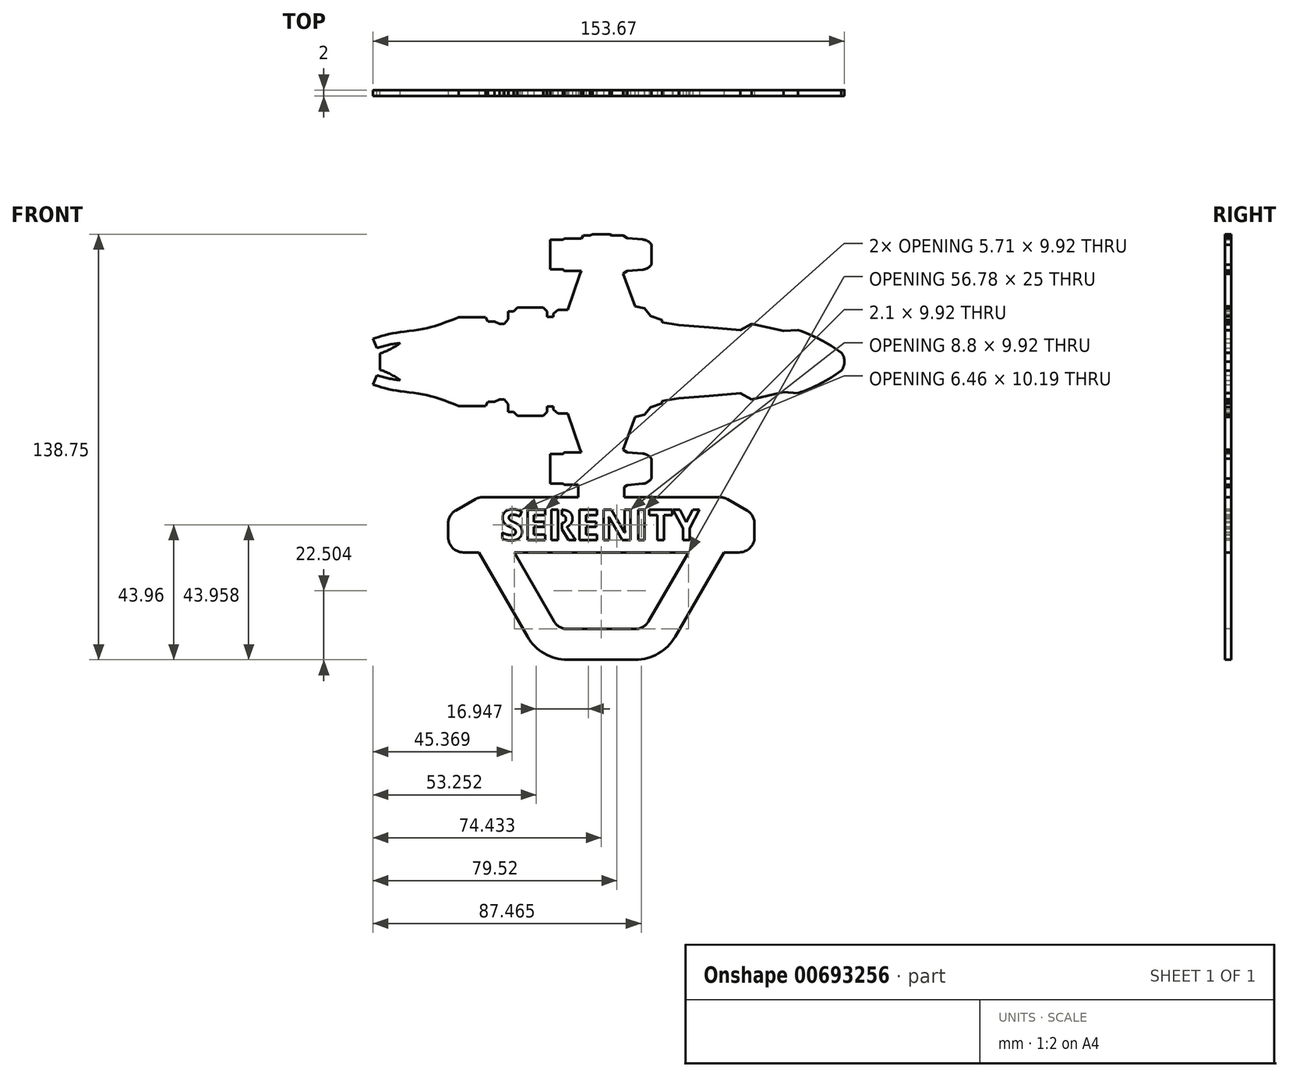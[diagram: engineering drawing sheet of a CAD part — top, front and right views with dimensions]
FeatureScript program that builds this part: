
annotation { "Feature Type Name" : "Feature", "Feature Type Description" : "" }
export const myFeature = defineFeature(function(context is Context, id is Id, definition is map)
    precondition{}
    {
        {
            var Q0;
            Q0=qCreatedBy(makeId("Front.planeOp"),FACE);
            var sketch = newSketch(context, id + "F0", { "sketchPlane" : qUnion([Q0])});
            skLineSegment(sketch, "E0", {"start": v(7.53, 23.83) * mm, "end": v(10.74, 15.17) * mm});
            skLineSegment(sketch, "E1", {"start": v(10.74, 15.17) * mm, "end": v(13.2, 14.62) * mm});
            skLineSegment(sketch, "E2", {"start": v(13.2, 14.62) * mm, "end": v(14.85, 12.63) * mm});
            skLineSegment(sketch, "E3", {"start": v(14.85, 12.63) * mm, "end": v(17.8, 11.6) * mm});
            skLineSegment(sketch, "E4", {"start": v(17.8, 11.6) * mm, "end": v(17.8, 10.91) * mm});
            skLineSegment(sketch, "E5", {"start": v(17.8, 10.91) * mm, "end": v(22.32, 10.23) * mm});
            skLineSegment(sketch, "E6", {"start": v(22.32, 10.23) * mm, "end": v(30.34, 9.58) * mm});
            skLineSegment(sketch, "E7", {"start": v(30.34, 9.58) * mm, "end": v(38.57, 8.93) * mm});
            skLineSegment(sketch, "E8", {"start": v(38.57, 8.93) * mm, "end": v(41.59, 10.56) * mm});
            skLineSegment(sketch, "E9", {"start": v(41.59, 10.56) * mm, "end": v(50.03, 8.63) * mm});
            skLineSegment(sketch, "E10", {"start": v(50.03, 8.63) * mm, "end": v(53.89, 8.9) * mm});
            skArc(sketch, "E11", {"start": v(65.33, 2.94) * mm, "mid": v(59.83, 6.35) * mm, "end": v(53.89, 8.9) * mm});
            skLineSegment(sketch, "E12", {"start": v(66.18, 0.52) * mm, "end": v(-57.02, 0.52) * mm, "construction": true});
            skArc(sketch, "E13", {"start": v(66.18, 0.52) * mm, "mid": v(65.97, 1.8) * mm, "end": v(65.33, 2.94) * mm});
            skLineSegment(sketch, "E14", {"start": v(7.53, 23.83) * mm, "end": v(8.61, 24.57) * mm});
            skLineSegment(sketch, "E15", {"start": v(8.61, 24.57) * mm, "end": v(12.67, 24.9) * mm});
            skArc(sketch, "E16", {"start": v(12.67, 24.9) * mm, "mid": v(14.02, 25.31) * mm, "end": v(15.04, 26.27) * mm});
            skLineSegment(sketch, "E17", {"start": v(15.04, 26.27) * mm, "end": v(15.04, 31.51) * mm});
            skLineSegment(sketch, "E18", {"start": v(15.04, 28.9) * mm, "end": v(-12.08, 28.9) * mm, "construction": true});
            skLineSegment(sketch, "E19", {"start": v(-3.95, 23.65) * mm, "end": v(-7.16, 14.3) * mm});
            skLineSegment(sketch, "E20", {"start": v(-3.95, 23.65) * mm, "end": v(-3.57, 24.6) * mm});
            skLineSegment(sketch, "E21", {"start": v(-3.57, 24.6) * mm, "end": v(-8.07, 24.6) * mm});
            skLineSegment(sketch, "E22", {"start": v(-8.07, 24.6) * mm, "end": v(-8.43, 24.95) * mm});
            skLineSegment(sketch, "E23", {"start": v(-8.43, 24.95) * mm, "end": v(-11.74, 24.95) * mm});
            skLineSegment(sketch, "E24", {"start": v(-11.74, 24.95) * mm, "end": v(-11.74, 32.83) * mm});
            skArc(sketch, "E25.MirrorCS", {"start": v(12.67, 32.9) * mm, "mid": v(14.02, 32.47) * mm, "end": v(15.04, 31.51) * mm});
            skLineSegment(sketch, "E26.MirrorCS", {"start": v(8.61, 33.21) * mm, "end": v(12.67, 32.9) * mm});
            skLineSegment(sketch, "E27.MirrorCS", {"start": v(7.53, 33.95) * mm, "end": v(8.61, 33.21) * mm});
            skLineSegment(sketch, "E28.MirrorCS", {"start": v(-3.57, 33.2) * mm, "end": v(-8.07, 33.2) * mm});
            skLineSegment(sketch, "E29.MirrorCS", {"start": v(-8.43, 32.83) * mm, "end": v(-11.74, 32.83) * mm});
            skLineSegment(sketch, "E30.MirrorCS", {"start": v(-8.07, 33.2) * mm, "end": v(-8.43, 32.83) * mm});
            skLineSegment(sketch, "E31", {"start": v(7.53, 33.95) * mm, "end": v(4.55, 33.95) * mm});
            skLineSegment(sketch, "E32", {"start": v(4.55, 33.95) * mm, "end": v(4, 34.32) * mm});
            skLineSegment(sketch, "E33", {"start": v(4, 34.32) * mm, "end": v(-0.49, 34.32) * mm});
            skLineSegment(sketch, "E34", {"start": v(-0.49, 34.32) * mm, "end": v(-1.24, 33.95) * mm});
            skLineSegment(sketch, "E35", {"start": v(-1.24, 33.95) * mm, "end": v(-3, 33.95) * mm});
            skLineSegment(sketch, "E36", {"start": v(-3, 33.95) * mm, "end": v(-3.57, 33.2) * mm});
            skLineSegment(sketch, "E37", {"start": v(-7.16, 14.3) * mm, "end": v(-9.7, 14.3) * mm});
            skLineSegment(sketch, "E38", {"start": v(-9.7, 14.3) * mm, "end": v(-10.96, 13.27) * mm});
            skLineSegment(sketch, "E39", {"start": v(-10.96, 13.27) * mm, "end": v(-10.96, 12.44) * mm});
            skLineSegment(sketch, "E40", {"start": v(-10.96, 12.44) * mm, "end": v(-12.6, 12.44) * mm});
            skLineSegment(sketch, "E41", {"start": v(-12.6, 12.44) * mm, "end": v(-12.6, 13.85) * mm});
            skLineSegment(sketch, "E42", {"start": v(-12.6, 13.85) * mm, "end": v(-13.62, 14.92) * mm});
            skLineSegment(sketch, "E43", {"start": v(-13.62, 14.92) * mm, "end": v(-20.41, 14.92) * mm});
            skLineSegment(sketch, "E44", {"start": v(-20.41, 14.92) * mm, "end": v(-21.53, 13.85) * mm});
            skLineSegment(sketch, "E45", {"start": v(-21.53, 13.85) * mm, "end": v(-22.98, 13.85) * mm});
            skLineSegment(sketch, "E46", {"start": v(-22.98, 13.85) * mm, "end": v(-22.98, 11.76) * mm});
            skLineSegment(sketch, "E47", {"start": v(-22.98, 11.76) * mm, "end": v(-23.95, 10.5) * mm});
            skLineSegment(sketch, "E48", {"start": v(-23.95, 10.5) * mm, "end": v(-25.26, 10.5) * mm});
            skLineSegment(sketch, "E49", {"start": v(-25.26, 10.5) * mm, "end": v(-26.52, 11.18) * mm});
            skLineSegment(sketch, "E50", {"start": v(-26.52, 11.18) * mm, "end": v(-28.31, 11.18) * mm});
            skLineSegment(sketch, "E51", {"start": v(-28.31, 11.18) * mm, "end": v(-28.94, 12.25) * mm});
            skLineSegment(sketch, "E52", {"start": v(-28.94, 12.25) * mm, "end": v(-36.05, 12.25) * mm});
            skFitSpline(sketch, "E53", {"points": [v(-36.05, 12.25) * mm, v(-38.85, 11.2) * mm, v(-41.9, 10.09) * mm, v(-45.19, 9.3) * mm, v(-50.09, 8.52) * mm, v(-53.77, 7.99) * mm, v(-56.87, 7.21) * mm, v(-58.76, 6.57) * mm], "startDerivative": vector(-20.36, -7.45) * mm, "endDerivative": vector(-15.85, -5.69) * mm});
            skArc(sketch, "E54", {"start": v(-56.96, 2.67) * mm, "mid": v(-54.13, 3.84) * mm, "end": v(-51.54, 5.44) * mm});
            skLineSegment(sketch, "E55", {"start": v(-56.96, 2.67) * mm, "end": v(-56.96, 0.52) * mm});
            skArc(sketch, "E56", {"start": v(-51.54, 5.44) * mm, "mid": v(-54.67, 4.96) * mm, "end": v(-57.73, 4.14) * mm});
            skLineSegment(sketch, "E57", {"start": v(-58.76, 6.57) * mm, "end": v(-57.73, 4.14) * mm});
            skLineSegment(sketch, "E58.MirrorCS", {"start": v(-8.07, -32.15) * mm, "end": v(-8.43, -31.79) * mm});
            skLineSegment(sketch, "E59.MirrorCS", {"start": v(-9.7, -13.25) * mm, "end": v(-10.96, -12.22) * mm});
            skLineSegment(sketch, "E60.MirrorCS", {"start": v(-8.43, -31.79) * mm, "end": v(-11.74, -31.79) * mm});
            skLineSegment(sketch, "E61.MirrorCS", {"start": v(-7.16, -13.25) * mm, "end": v(-9.7, -13.25) * mm});
            skLineSegment(sketch, "E62.MirrorCS", {"start": v(-58.76, -5.53) * mm, "end": v(-57.73, -3.1) * mm});
            skLineSegment(sketch, "E63.MirrorCS", {"start": v(4.55, -32.9) * mm, "end": v(4, -33.27) * mm});
            skLineSegment(sketch, "E64.MirrorCS", {"start": v(4, -33.27) * mm, "end": v(-0.49, -33.27) * mm});
            skLineSegment(sketch, "E65.MirrorCS", {"start": v(7.53, -32.9) * mm, "end": v(4.55, -32.9) * mm});
            skLineSegment(sketch, "E66.MirrorCS", {"start": v(-28.31, -10.14) * mm, "end": v(-28.94, -11.2) * mm});
            skLineSegment(sketch, "E67.MirrorCS", {"start": v(-3.57, -32.15) * mm, "end": v(-8.07, -32.15) * mm});
            skLineSegment(sketch, "E68.MirrorCS", {"start": v(-10.96, -12.22) * mm, "end": v(-10.96, -11.4) * mm});
            skLineSegment(sketch, "E69.MirrorCS", {"start": v(14.85, -11.59) * mm, "end": v(17.8, -10.56) * mm});
            skLineSegment(sketch, "E70.MirrorCS", {"start": v(17.8, -10.56) * mm, "end": v(17.8, -9.87) * mm});
            skLineSegment(sketch, "E71.MirrorCS", {"start": v(-3.95, -22.6) * mm, "end": v(-3.57, -23.55) * mm});
            skLineSegment(sketch, "E72.MirrorCS", {"start": v(-10.96, -11.4) * mm, "end": v(-12.6, -11.4) * mm});
            skLineSegment(sketch, "E73.MirrorCS", {"start": v(-8.07, -23.55) * mm, "end": v(-8.43, -23.9) * mm});
            skLineSegment(sketch, "E74.MirrorCS", {"start": v(7.53, -32.9) * mm, "end": v(8.61, -32.17) * mm});
            skLineSegment(sketch, "E75.MirrorCS", {"start": v(-0.49, -33.27) * mm, "end": v(-1.24, -32.9) * mm});
            skLineSegment(sketch, "E76.MirrorCS", {"start": v(-26.52, -10.14) * mm, "end": v(-28.31, -10.14) * mm});
            skLineSegment(sketch, "E77.MirrorCS", {"start": v(-22.98, -10.72) * mm, "end": v(-23.95, -9.46) * mm});
            skLineSegment(sketch, "E78.MirrorCS", {"start": v(-23.95, -9.46) * mm, "end": v(-25.26, -9.46) * mm});
            skLineSegment(sketch, "E79.MirrorCS", {"start": v(-25.26, -9.46) * mm, "end": v(-26.52, -10.14) * mm});
            skLineSegment(sketch, "E80.MirrorCS", {"start": v(-12.6, -12.8) * mm, "end": v(-13.62, -13.87) * mm});
            skLineSegment(sketch, "E81.MirrorCS", {"start": v(-20.41, -13.87) * mm, "end": v(-21.53, -12.8) * mm});
            skLineSegment(sketch, "E82.MirrorCS", {"start": v(-1.24, -32.9) * mm, "end": v(-3, -32.9) * mm});
            skLineSegment(sketch, "E83.MirrorCS", {"start": v(-56.96, -1.63) * mm, "end": v(-56.96, 0.52) * mm});
            skLineSegment(sketch, "E84.MirrorCS", {"start": v(-28.94, -11.2) * mm, "end": v(-36.05, -11.2) * mm});
            skLineSegment(sketch, "E85.MirrorCS", {"start": v(-3, -32.9) * mm, "end": v(-3.57, -32.15) * mm});
            skLineSegment(sketch, "E86.MirrorCS", {"start": v(17.8, -9.87) * mm, "end": v(22.32, -9.18) * mm});
            skLineSegment(sketch, "E87.MirrorCS", {"start": v(-22.98, -12.8) * mm, "end": v(-22.98, -10.72) * mm});
            skArc(sketch, "E88.MirrorCS", {"start": v(-56.96, -1.63) * mm, "mid": v(-54.13, -2.8) * mm, "end": v(-51.54, -4.4) * mm});
            skLineSegment(sketch, "E89.MirrorCS", {"start": v(7.53, -22.79) * mm, "end": v(8.61, -23.53) * mm});
            skLineSegment(sketch, "E90.MirrorCS", {"start": v(-13.62, -13.87) * mm, "end": v(-20.41, -13.87) * mm});
            skLineSegment(sketch, "E91.MirrorCS", {"start": v(-3.57, -23.55) * mm, "end": v(-8.07, -23.55) * mm});
            skLineSegment(sketch, "E92.MirrorCS", {"start": v(-21.53, -12.8) * mm, "end": v(-22.98, -12.8) * mm});
            skLineSegment(sketch, "E93.MirrorCS", {"start": v(8.61, -23.53) * mm, "end": v(12.67, -23.85) * mm});
            skArc(sketch, "E94.MirrorCS", {"start": v(66.18, 0.52) * mm, "mid": v(65.97, -0.76) * mm, "end": v(65.33, -1.9) * mm});
            skLineSegment(sketch, "E95.MirrorCS", {"start": v(8.61, -32.17) * mm, "end": v(12.67, -31.85) * mm});
            skLineSegment(sketch, "E96.MirrorCS", {"start": v(-12.6, -11.4) * mm, "end": v(-12.6, -12.8) * mm});
            skArc(sketch, "E97.MirrorCS", {"start": v(12.67, -31.85) * mm, "mid": v(14.02, -31.43) * mm, "end": v(15.04, -30.47) * mm});
            skLineSegment(sketch, "E98.MirrorCS", {"start": v(41.59, -9.52) * mm, "end": v(50.03, -7.58) * mm});
            skArc(sketch, "E99.MirrorCS", {"start": v(12.67, -23.85) * mm, "mid": v(14.02, -24.27) * mm, "end": v(15.04, -25.23) * mm});
            skLineSegment(sketch, "E100.MirrorCS", {"start": v(50.03, -7.58) * mm, "end": v(53.89, -7.86) * mm});
            skLineSegment(sketch, "E101.MirrorCS", {"start": v(-8.43, -23.9) * mm, "end": v(-11.74, -23.9) * mm});
            skLineSegment(sketch, "E102.MirrorCS", {"start": v(15.04, -25.23) * mm, "end": v(15.04, -30.47) * mm});
            skLineSegment(sketch, "E103.MirrorCS", {"start": v(-11.74, -23.9) * mm, "end": v(-11.74, -31.79) * mm});
            skArc(sketch, "E104.MirrorCS", {"start": v(-51.54, -4.4) * mm, "mid": v(-54.67, -3.91) * mm, "end": v(-57.73, -3.1) * mm});
            skLineSegment(sketch, "E105.MirrorCS", {"start": v(38.57, -7.88) * mm, "end": v(41.59, -9.52) * mm});
            skLineSegment(sketch, "E106.MirrorCS", {"start": v(22.32, -9.18) * mm, "end": v(30.34, -8.54) * mm});
            skLineSegment(sketch, "E107.MirrorCS", {"start": v(10.74, -14.13) * mm, "end": v(13.2, -13.58) * mm});
            skLineSegment(sketch, "E108.MirrorCS", {"start": v(13.2, -13.58) * mm, "end": v(14.85, -11.59) * mm});
            skFitSpline(sketch, "E109.MirrorCS", {"points": [v(-36.05, -11.2) * mm, v(-38.85, -10.16) * mm, v(-41.9, -9.05) * mm, v(-45.19, -8.25) * mm, v(-50.09, -7.48) * mm, v(-53.77, -6.94) * mm, v(-56.87, -6.17) * mm, v(-58.76, -5.53) * mm], "startDerivative": vector(-20.36, 7.45) * mm, "endDerivative": vector(-15.85, 5.69) * mm});
            skLineSegment(sketch, "E110.MirrorCS", {"start": v(15.04, -27.85) * mm, "end": v(-12.08, -27.85) * mm, "construction": true});
            skArc(sketch, "E111.MirrorCS", {"start": v(65.33, -1.9) * mm, "mid": v(59.83, -5.3) * mm, "end": v(53.89, -7.86) * mm});
            skLineSegment(sketch, "E112.MirrorCS", {"start": v(-3.95, -22.6) * mm, "end": v(-7.16, -13.25) * mm});
            skLineSegment(sketch, "E113.MirrorCS", {"start": v(7.53, -22.79) * mm, "end": v(10.74, -14.13) * mm});
            skLineSegment(sketch, "E114.MirrorCS", {"start": v(30.34, -8.54) * mm, "end": v(38.57, -7.88) * mm});
            skSolve(sketch);
        }
        {
            var Q0;
            Q0 = qSketchRegion(id + "F0", true);
            extrude(context, id + "F1", {"entities" : qUnion([Q0]), "depth" : 2 * mm, "offsetDistance" : 25 * mm});
        }
        {
            var Q0;
            Q0=makeQuery(id+"F1.opExtrude","SWEPT_BODY",BODY,{"disambiguationData":[OSD([sQuery(id+"F0.wireOp",EDGE,"E0"),sQuery(id+"F0.wireOp",EDGE,"E1"),sQuery(id+"F0.wireOp",EDGE,"E2"),sQuery(id+"F0.wireOp",EDGE,"E3"),sQuery(id+"F0.wireOp",EDGE,"E4"),sQuery(id+"F0.wireOp",EDGE,"E5"),sQuery(id+"F0.wireOp",EDGE,"E6"),sQuery(id+"F0.wireOp",EDGE,"E7"),sQuery(id+"F0.wireOp",EDGE,"E8"),sQuery(id+"F0.wireOp",EDGE,"E9"),sQuery(id+"F0.wireOp",EDGE,"E10"),sQuery(id+"F0.wireOp",EDGE,"E11"),sQuery(id+"F0.wireOp",EDGE,"E13"),sQuery(id+"F0.wireOp",EDGE,"E14"),sQuery(id+"F0.wireOp",EDGE,"E15"),sQuery(id+"F0.wireOp",EDGE,"E16"),sQuery(id+"F0.wireOp",EDGE,"E17"),sQuery(id+"F0.wireOp",EDGE,"E19"),sQuery(id+"F0.wireOp",EDGE,"E20"),sQuery(id+"F0.wireOp",EDGE,"E21"),sQuery(id+"F0.wireOp",EDGE,"E22"),sQuery(id+"F0.wireOp",EDGE,"E23"),sQuery(id+"F0.wireOp",EDGE,"E24"),sQuery(id+"F0.wireOp",EDGE,"E25.MirrorCS"),sQuery(id+"F0.wireOp",EDGE,"E26.MirrorCS"),sQuery(id+"F0.wireOp",EDGE,"E27.MirrorCS"),sQuery(id+"F0.wireOp",EDGE,"E28.MirrorCS"),sQuery(id+"F0.wireOp",EDGE,"E29.MirrorCS"),sQuery(id+"F0.wireOp",EDGE,"E30.MirrorCS"),sQuery(id+"F0.wireOp",EDGE,"E31"),sQuery(id+"F0.wireOp",EDGE,"E32"),sQuery(id+"F0.wireOp",EDGE,"E33"),sQuery(id+"F0.wireOp",EDGE,"E34"),sQuery(id+"F0.wireOp",EDGE,"E35"),sQuery(id+"F0.wireOp",EDGE,"E36"),sQuery(id+"F0.wireOp",EDGE,"E37"),sQuery(id+"F0.wireOp",EDGE,"E38"),sQuery(id+"F0.wireOp",EDGE,"E39"),sQuery(id+"F0.wireOp",EDGE,"E40"),sQuery(id+"F0.wireOp",EDGE,"E41"),sQuery(id+"F0.wireOp",EDGE,"E42"),sQuery(id+"F0.wireOp",EDGE,"E43"),sQuery(id+"F0.wireOp",EDGE,"E44"),sQuery(id+"F0.wireOp",EDGE,"E45"),sQuery(id+"F0.wireOp",EDGE,"E46"),sQuery(id+"F0.wireOp",EDGE,"E47"),sQuery(id+"F0.wireOp",EDGE,"E48"),sQuery(id+"F0.wireOp",EDGE,"E49"),sQuery(id+"F0.wireOp",EDGE,"E50"),sQuery(id+"F0.wireOp",EDGE,"E51"),sQuery(id+"F0.wireOp",EDGE,"E52"),sQuery(id+"F0.wireOp",EDGE,"E53"),sQuery(id+"F0.wireOp",EDGE,"E54"),sQuery(id+"F0.wireOp",EDGE,"E55"),sQuery(id+"F0.wireOp",EDGE,"E56"),sQuery(id+"F0.wireOp",EDGE,"E57"),sQuery(id+"F0.wireOp",EDGE,"E58.MirrorCS"),sQuery(id+"F0.wireOp",EDGE,"E59.MirrorCS"),sQuery(id+"F0.wireOp",EDGE,"E60.MirrorCS"),sQuery(id+"F0.wireOp",EDGE,"E61.MirrorCS"),sQuery(id+"F0.wireOp",EDGE,"E62.MirrorCS"),sQuery(id+"F0.wireOp",EDGE,"E63.MirrorCS"),sQuery(id+"F0.wireOp",EDGE,"E64.MirrorCS"),sQuery(id+"F0.wireOp",EDGE,"E65.MirrorCS"),sQuery(id+"F0.wireOp",EDGE,"E66.MirrorCS"),sQuery(id+"F0.wireOp",EDGE,"E67.MirrorCS"),sQuery(id+"F0.wireOp",EDGE,"E68.MirrorCS"),sQuery(id+"F0.wireOp",EDGE,"E69.MirrorCS"),sQuery(id+"F0.wireOp",EDGE,"E70.MirrorCS"),sQuery(id+"F0.wireOp",EDGE,"E71.MirrorCS"),sQuery(id+"F0.wireOp",EDGE,"E72.MirrorCS"),sQuery(id+"F0.wireOp",EDGE,"E73.MirrorCS"),sQuery(id+"F0.wireOp",EDGE,"E74.MirrorCS"),sQuery(id+"F0.wireOp",EDGE,"E75.MirrorCS"),sQuery(id+"F0.wireOp",EDGE,"E76.MirrorCS"),sQuery(id+"F0.wireOp",EDGE,"E77.MirrorCS"),sQuery(id+"F0.wireOp",EDGE,"E78.MirrorCS"),sQuery(id+"F0.wireOp",EDGE,"E79.MirrorCS"),sQuery(id+"F0.wireOp",EDGE,"E80.MirrorCS"),sQuery(id+"F0.wireOp",EDGE,"E81.MirrorCS"),sQuery(id+"F0.wireOp",EDGE,"E82.MirrorCS"),sQuery(id+"F0.wireOp",EDGE,"E83.MirrorCS"),sQuery(id+"F0.wireOp",EDGE,"E84.MirrorCS"),sQuery(id+"F0.wireOp",EDGE,"E85.MirrorCS"),sQuery(id+"F0.wireOp",EDGE,"E86.MirrorCS"),sQuery(id+"F0.wireOp",EDGE,"E87.MirrorCS"),sQuery(id+"F0.wireOp",EDGE,"E88.MirrorCS"),sQuery(id+"F0.wireOp",EDGE,"E89.MirrorCS"),sQuery(id+"F0.wireOp",EDGE,"E90.MirrorCS"),sQuery(id+"F0.wireOp",EDGE,"E91.MirrorCS"),sQuery(id+"F0.wireOp",EDGE,"E92.MirrorCS"),sQuery(id+"F0.wireOp",EDGE,"E93.MirrorCS"),sQuery(id+"F0.wireOp",EDGE,"E94.MirrorCS"),sQuery(id+"F0.wireOp",EDGE,"E95.MirrorCS"),sQuery(id+"F0.wireOp",EDGE,"E96.MirrorCS"),sQuery(id+"F0.wireOp",EDGE,"E97.MirrorCS"),sQuery(id+"F0.wireOp",EDGE,"E98.MirrorCS"),sQuery(id+"F0.wireOp",EDGE,"E99.MirrorCS"),sQuery(id+"F0.wireOp",EDGE,"E100.MirrorCS"),sQuery(id+"F0.wireOp",EDGE,"E101.MirrorCS"),sQuery(id+"F0.wireOp",EDGE,"E102.MirrorCS"),sQuery(id+"F0.wireOp",EDGE,"E103.MirrorCS"),sQuery(id+"F0.wireOp",EDGE,"E104.MirrorCS"),sQuery(id+"F0.wireOp",EDGE,"E105.MirrorCS"),sQuery(id+"F0.wireOp",EDGE,"E106.MirrorCS"),sQuery(id+"F0.wireOp",EDGE,"E107.MirrorCS"),sQuery(id+"F0.wireOp",EDGE,"E108.MirrorCS"),sQuery(id+"F0.wireOp",EDGE,"E109.MirrorCS"),sQuery(id+"F0.wireOp",EDGE,"E111.MirrorCS"),sQuery(id+"F0.wireOp",EDGE,"E112.MirrorCS"),sQuery(id+"F0.wireOp",EDGE,"E113.MirrorCS"),sQuery(id+"F0.wireOp",EDGE,"E114.MirrorCS")])]});
            var Q1;
            Q1=makeQuery(id+"F1.opExtrude","CAP_VERTEX",VERTEX,{"disambiguationData":[OSD([sQuery(id+"F0.wireOp",EDGE,"E83.MirrorCS"),sQuery(id+"F0.wireOp",EDGE,"E88.MirrorCS")])],"isStart":false});
            transform(context, id + "F2", {"entities" : qUnion([Q0]), "transformType" : TransformType.SCALE_UNIFORMLY, "scale" : 1.23, "scalePoint" : qUnion([Q1]), "makeCopy" : false});
        }
        {
            var Q0;
            Q0=makeQuery(id+"F1.opExtrude","CAP_FACE",FACE,{"disambiguationData":[OSD([sQuery(id+"F0.wireOp",EDGE,"E0"),sQuery(id+"F0.wireOp",EDGE,"E1"),sQuery(id+"F0.wireOp",EDGE,"E2"),sQuery(id+"F0.wireOp",EDGE,"E3"),sQuery(id+"F0.wireOp",EDGE,"E4"),sQuery(id+"F0.wireOp",EDGE,"E5"),sQuery(id+"F0.wireOp",EDGE,"E6"),sQuery(id+"F0.wireOp",EDGE,"E7"),sQuery(id+"F0.wireOp",EDGE,"E8"),sQuery(id+"F0.wireOp",EDGE,"E9"),sQuery(id+"F0.wireOp",EDGE,"E10"),sQuery(id+"F0.wireOp",EDGE,"E11"),sQuery(id+"F0.wireOp",EDGE,"E13"),sQuery(id+"F0.wireOp",EDGE,"E14"),sQuery(id+"F0.wireOp",EDGE,"E15"),sQuery(id+"F0.wireOp",EDGE,"E16"),sQuery(id+"F0.wireOp",EDGE,"E17"),sQuery(id+"F0.wireOp",EDGE,"E19"),sQuery(id+"F0.wireOp",EDGE,"E20"),sQuery(id+"F0.wireOp",EDGE,"E21"),sQuery(id+"F0.wireOp",EDGE,"E22"),sQuery(id+"F0.wireOp",EDGE,"E23"),sQuery(id+"F0.wireOp",EDGE,"E24"),sQuery(id+"F0.wireOp",EDGE,"E25.MirrorCS"),sQuery(id+"F0.wireOp",EDGE,"E26.MirrorCS"),sQuery(id+"F0.wireOp",EDGE,"E27.MirrorCS"),sQuery(id+"F0.wireOp",EDGE,"E28.MirrorCS"),sQuery(id+"F0.wireOp",EDGE,"E29.MirrorCS"),sQuery(id+"F0.wireOp",EDGE,"E30.MirrorCS"),sQuery(id+"F0.wireOp",EDGE,"E31"),sQuery(id+"F0.wireOp",EDGE,"E32"),sQuery(id+"F0.wireOp",EDGE,"E33"),sQuery(id+"F0.wireOp",EDGE,"E34"),sQuery(id+"F0.wireOp",EDGE,"E35"),sQuery(id+"F0.wireOp",EDGE,"E36"),sQuery(id+"F0.wireOp",EDGE,"E37"),sQuery(id+"F0.wireOp",EDGE,"E38"),sQuery(id+"F0.wireOp",EDGE,"E39"),sQuery(id+"F0.wireOp",EDGE,"E40"),sQuery(id+"F0.wireOp",EDGE,"E41"),sQuery(id+"F0.wireOp",EDGE,"E42"),sQuery(id+"F0.wireOp",EDGE,"E43"),sQuery(id+"F0.wireOp",EDGE,"E44"),sQuery(id+"F0.wireOp",EDGE,"E45"),sQuery(id+"F0.wireOp",EDGE,"E46"),sQuery(id+"F0.wireOp",EDGE,"E47"),sQuery(id+"F0.wireOp",EDGE,"E48"),sQuery(id+"F0.wireOp",EDGE,"E49"),sQuery(id+"F0.wireOp",EDGE,"E50"),sQuery(id+"F0.wireOp",EDGE,"E51"),sQuery(id+"F0.wireOp",EDGE,"E52"),sQuery(id+"F0.wireOp",EDGE,"E53"),sQuery(id+"F0.wireOp",EDGE,"E54"),sQuery(id+"F0.wireOp",EDGE,"E55"),sQuery(id+"F0.wireOp",EDGE,"E56"),sQuery(id+"F0.wireOp",EDGE,"E57"),sQuery(id+"F0.wireOp",EDGE,"E58.MirrorCS"),sQuery(id+"F0.wireOp",EDGE,"E59.MirrorCS"),sQuery(id+"F0.wireOp",EDGE,"E60.MirrorCS"),sQuery(id+"F0.wireOp",EDGE,"E61.MirrorCS"),sQuery(id+"F0.wireOp",EDGE,"E62.MirrorCS"),sQuery(id+"F0.wireOp",EDGE,"E63.MirrorCS"),sQuery(id+"F0.wireOp",EDGE,"E64.MirrorCS"),sQuery(id+"F0.wireOp",EDGE,"E65.MirrorCS"),sQuery(id+"F0.wireOp",EDGE,"E66.MirrorCS"),sQuery(id+"F0.wireOp",EDGE,"E67.MirrorCS"),sQuery(id+"F0.wireOp",EDGE,"E68.MirrorCS"),sQuery(id+"F0.wireOp",EDGE,"E69.MirrorCS"),sQuery(id+"F0.wireOp",EDGE,"E70.MirrorCS"),sQuery(id+"F0.wireOp",EDGE,"E71.MirrorCS"),sQuery(id+"F0.wireOp",EDGE,"E72.MirrorCS"),sQuery(id+"F0.wireOp",EDGE,"E73.MirrorCS"),sQuery(id+"F0.wireOp",EDGE,"E74.MirrorCS"),sQuery(id+"F0.wireOp",EDGE,"E75.MirrorCS"),sQuery(id+"F0.wireOp",EDGE,"E76.MirrorCS"),sQuery(id+"F0.wireOp",EDGE,"E77.MirrorCS"),sQuery(id+"F0.wireOp",EDGE,"E78.MirrorCS"),sQuery(id+"F0.wireOp",EDGE,"E79.MirrorCS"),sQuery(id+"F0.wireOp",EDGE,"E80.MirrorCS"),sQuery(id+"F0.wireOp",EDGE,"E81.MirrorCS"),sQuery(id+"F0.wireOp",EDGE,"E82.MirrorCS"),sQuery(id+"F0.wireOp",EDGE,"E83.MirrorCS"),sQuery(id+"F0.wireOp",EDGE,"E84.MirrorCS"),sQuery(id+"F0.wireOp",EDGE,"E85.MirrorCS"),sQuery(id+"F0.wireOp",EDGE,"E86.MirrorCS"),sQuery(id+"F0.wireOp",EDGE,"E87.MirrorCS"),sQuery(id+"F0.wireOp",EDGE,"E88.MirrorCS"),sQuery(id+"F0.wireOp",EDGE,"E89.MirrorCS"),sQuery(id+"F0.wireOp",EDGE,"E90.MirrorCS"),sQuery(id+"F0.wireOp",EDGE,"E91.MirrorCS"),sQuery(id+"F0.wireOp",EDGE,"E92.MirrorCS"),sQuery(id+"F0.wireOp",EDGE,"E93.MirrorCS"),sQuery(id+"F0.wireOp",EDGE,"E94.MirrorCS"),sQuery(id+"F0.wireOp",EDGE,"E95.MirrorCS"),sQuery(id+"F0.wireOp",EDGE,"E96.MirrorCS"),sQuery(id+"F0.wireOp",EDGE,"E97.MirrorCS"),sQuery(id+"F0.wireOp",EDGE,"E98.MirrorCS"),sQuery(id+"F0.wireOp",EDGE,"E99.MirrorCS"),sQuery(id+"F0.wireOp",EDGE,"E100.MirrorCS"),sQuery(id+"F0.wireOp",EDGE,"E101.MirrorCS"),sQuery(id+"F0.wireOp",EDGE,"E102.MirrorCS"),sQuery(id+"F0.wireOp",EDGE,"E103.MirrorCS"),sQuery(id+"F0.wireOp",EDGE,"E104.MirrorCS"),sQuery(id+"F0.wireOp",EDGE,"E105.MirrorCS"),sQuery(id+"F0.wireOp",EDGE,"E106.MirrorCS"),sQuery(id+"F0.wireOp",EDGE,"E107.MirrorCS"),sQuery(id+"F0.wireOp",EDGE,"E108.MirrorCS"),sQuery(id+"F0.wireOp",EDGE,"E109.MirrorCS"),sQuery(id+"F0.wireOp",EDGE,"E111.MirrorCS"),sQuery(id+"F0.wireOp",EDGE,"E112.MirrorCS"),sQuery(id+"F0.wireOp",EDGE,"E113.MirrorCS"),sQuery(id+"F0.wireOp",EDGE,"E114.MirrorCS")])],"isStart":false});
            var sketch = newSketch(context, id + "F3", { "sketchPlane" : qUnion([Q0])});
            skLineSegment(sketch, "E115.bottom", {"start": v(7.76, -37.17) * mm, "end": v(22.76, -37.17) * mm});
            skLineSegment(sketch, "E115.top", {"start": v(7.76, -43.17) * mm, "end": v(22.76, -43.17) * mm});
            skLineSegment(sketch, "E115.left", {"start": v(7.76, -37.17) * mm, "end": v(7.76, -43.17) * mm});
            skLineSegment(sketch, "E115.right", {"start": v(22.76, -37.17) * mm, "end": v(22.76, -43.17) * mm});
            skLineSegment(sketch, "E116", {"start": v(15.26, -40.55) * mm, "end": v(15.26, -37.17) * mm, "construction": true});
            skLineSegment(sketch, "E117", {"start": v(7.76, -43.17) * mm, "end": v(-24.67, -43.17) * mm});
            skLineSegment(sketch, "E118", {"start": v(-24.67, -43.17) * mm, "end": v(-34.67, -48.94) * mm});
            skLineSegment(sketch, "E119", {"start": v(-34.67, -48.94) * mm, "end": v(-34.67, -61.17) * mm});
            skLineSegment(sketch, "E120.MirrorCS", {"start": v(22.76, -43.17) * mm, "end": v(55.2, -43.17) * mm});
            skLineSegment(sketch, "E121.MirrorCS", {"start": v(55.2, -43.17) * mm, "end": v(65.2, -48.94) * mm});
            skLineSegment(sketch, "E122.MirrorCS", {"start": v(65.2, -48.94) * mm, "end": v(65.2, -61.17) * mm});
            skLineSegment(sketch, "E123", {"start": v(-34.67, -61.17) * mm, "end": v(65.2, -61.17) * mm});
            skText(sketch, "E124", { "text": "SERENITY", "fontName": "OpenSans-Bold.ttf"});
            skLineSegment(sketch, "E125", {"start": v(-24.67, -61.17) * mm, "end": v(-4.47, -96.17) * mm});
            skLineSegment(sketch, "E126", {"start": v(-4.47, -96.17) * mm, "end": v(35, -96.17) * mm});
            skLineSegment(sketch, "E127", {"start": v(35, -96.17) * mm, "end": v(55.2, -61.17) * mm});
            skLineSegment(sketch, "E128.0", {"start": v(29.22, -86.17) * mm, "end": v(43.65, -61.17) * mm});
            skLineSegment(sketch, "E128.1", {"start": v(1.3, -86.17) * mm, "end": v(29.22, -86.17) * mm});
            skLineSegment(sketch, "E128.2", {"start": v(-13.13, -61.17) * mm, "end": v(1.3, -86.17) * mm});
            const initialGuessF3  = {"E124": [-0.01767, -0.05717, 1, 0, 0.01]};
            skSetInitialGuess(sketch, initialGuessF3);
            skSolve(sketch);
        }
        {
            var Q0;
            {var subQ3=sQuery(id+"F3.wireOp",EDGE,"E125");Q0=makeQuery(id+"F3.imprint","IMPRINT",FACE,{"disambiguationData":[TD([[makeQuery(id+"F3.imprint","IMPRINT",EDGE,{"derivedFrom":subQ3}),1.0]])]});}
            var Q1;
            Q1=makeQuery(id+"F3.imprint","IMPRINT",FACE,{"disambiguationData":[TD([[makeQuery(id+"F3.imprint","IMPRINT",EDGE,{"derivedFrom":sQuery(id+"F3.wireOp",EDGE,"E115.top")}),-1.0]])]});
            var Q2;
            {var subQ4=sQuery(id+"F3.wireOp",EDGE,"E115.top");Q2=makeQuery(id+"F3.imprint","IMPRINT",FACE,{"disambiguationData":[TD([[makeQuery(id+"F3.imprint","IMPRINT",EDGE,{"derivedFrom":subQ4}),1.0]])]});}
            var Q3;
            Q3=makeQuery(id+"F1.opExtrude","CAP_FACE",FACE,{"disambiguationData":[OSD([sQuery(id+"F0.wireOp",EDGE,"E0"),sQuery(id+"F0.wireOp",EDGE,"E1"),sQuery(id+"F0.wireOp",EDGE,"E2"),sQuery(id+"F0.wireOp",EDGE,"E3"),sQuery(id+"F0.wireOp",EDGE,"E4"),sQuery(id+"F0.wireOp",EDGE,"E5"),sQuery(id+"F0.wireOp",EDGE,"E6"),sQuery(id+"F0.wireOp",EDGE,"E7"),sQuery(id+"F0.wireOp",EDGE,"E8"),sQuery(id+"F0.wireOp",EDGE,"E9"),sQuery(id+"F0.wireOp",EDGE,"E10"),sQuery(id+"F0.wireOp",EDGE,"E11"),sQuery(id+"F0.wireOp",EDGE,"E13"),sQuery(id+"F0.wireOp",EDGE,"E14"),sQuery(id+"F0.wireOp",EDGE,"E15"),sQuery(id+"F0.wireOp",EDGE,"E16"),sQuery(id+"F0.wireOp",EDGE,"E17"),sQuery(id+"F0.wireOp",EDGE,"E19"),sQuery(id+"F0.wireOp",EDGE,"E20"),sQuery(id+"F0.wireOp",EDGE,"E21"),sQuery(id+"F0.wireOp",EDGE,"E22"),sQuery(id+"F0.wireOp",EDGE,"E23"),sQuery(id+"F0.wireOp",EDGE,"E24"),sQuery(id+"F0.wireOp",EDGE,"E25.MirrorCS"),sQuery(id+"F0.wireOp",EDGE,"E26.MirrorCS"),sQuery(id+"F0.wireOp",EDGE,"E27.MirrorCS"),sQuery(id+"F0.wireOp",EDGE,"E28.MirrorCS"),sQuery(id+"F0.wireOp",EDGE,"E29.MirrorCS"),sQuery(id+"F0.wireOp",EDGE,"E30.MirrorCS"),sQuery(id+"F0.wireOp",EDGE,"E31"),sQuery(id+"F0.wireOp",EDGE,"E32"),sQuery(id+"F0.wireOp",EDGE,"E33"),sQuery(id+"F0.wireOp",EDGE,"E34"),sQuery(id+"F0.wireOp",EDGE,"E35"),sQuery(id+"F0.wireOp",EDGE,"E36"),sQuery(id+"F0.wireOp",EDGE,"E37"),sQuery(id+"F0.wireOp",EDGE,"E38"),sQuery(id+"F0.wireOp",EDGE,"E39"),sQuery(id+"F0.wireOp",EDGE,"E40"),sQuery(id+"F0.wireOp",EDGE,"E41"),sQuery(id+"F0.wireOp",EDGE,"E42"),sQuery(id+"F0.wireOp",EDGE,"E43"),sQuery(id+"F0.wireOp",EDGE,"E44"),sQuery(id+"F0.wireOp",EDGE,"E45"),sQuery(id+"F0.wireOp",EDGE,"E46"),sQuery(id+"F0.wireOp",EDGE,"E47"),sQuery(id+"F0.wireOp",EDGE,"E48"),sQuery(id+"F0.wireOp",EDGE,"E49"),sQuery(id+"F0.wireOp",EDGE,"E50"),sQuery(id+"F0.wireOp",EDGE,"E51"),sQuery(id+"F0.wireOp",EDGE,"E52"),sQuery(id+"F0.wireOp",EDGE,"E53"),sQuery(id+"F0.wireOp",EDGE,"E54"),sQuery(id+"F0.wireOp",EDGE,"E55"),sQuery(id+"F0.wireOp",EDGE,"E56"),sQuery(id+"F0.wireOp",EDGE,"E57"),sQuery(id+"F0.wireOp",EDGE,"E58.MirrorCS"),sQuery(id+"F0.wireOp",EDGE,"E59.MirrorCS"),sQuery(id+"F0.wireOp",EDGE,"E60.MirrorCS"),sQuery(id+"F0.wireOp",EDGE,"E61.MirrorCS"),sQuery(id+"F0.wireOp",EDGE,"E62.MirrorCS"),sQuery(id+"F0.wireOp",EDGE,"E63.MirrorCS"),sQuery(id+"F0.wireOp",EDGE,"E64.MirrorCS"),sQuery(id+"F0.wireOp",EDGE,"E65.MirrorCS"),sQuery(id+"F0.wireOp",EDGE,"E66.MirrorCS"),sQuery(id+"F0.wireOp",EDGE,"E67.MirrorCS"),sQuery(id+"F0.wireOp",EDGE,"E68.MirrorCS"),sQuery(id+"F0.wireOp",EDGE,"E69.MirrorCS"),sQuery(id+"F0.wireOp",EDGE,"E70.MirrorCS"),sQuery(id+"F0.wireOp",EDGE,"E71.MirrorCS"),sQuery(id+"F0.wireOp",EDGE,"E72.MirrorCS"),sQuery(id+"F0.wireOp",EDGE,"E73.MirrorCS"),sQuery(id+"F0.wireOp",EDGE,"E74.MirrorCS"),sQuery(id+"F0.wireOp",EDGE,"E75.MirrorCS"),sQuery(id+"F0.wireOp",EDGE,"E76.MirrorCS"),sQuery(id+"F0.wireOp",EDGE,"E77.MirrorCS"),sQuery(id+"F0.wireOp",EDGE,"E78.MirrorCS"),sQuery(id+"F0.wireOp",EDGE,"E79.MirrorCS"),sQuery(id+"F0.wireOp",EDGE,"E80.MirrorCS"),sQuery(id+"F0.wireOp",EDGE,"E81.MirrorCS"),sQuery(id+"F0.wireOp",EDGE,"E82.MirrorCS"),sQuery(id+"F0.wireOp",EDGE,"E83.MirrorCS"),sQuery(id+"F0.wireOp",EDGE,"E84.MirrorCS"),sQuery(id+"F0.wireOp",EDGE,"E85.MirrorCS"),sQuery(id+"F0.wireOp",EDGE,"E86.MirrorCS"),sQuery(id+"F0.wireOp",EDGE,"E87.MirrorCS"),sQuery(id+"F0.wireOp",EDGE,"E88.MirrorCS"),sQuery(id+"F0.wireOp",EDGE,"E89.MirrorCS"),sQuery(id+"F0.wireOp",EDGE,"E90.MirrorCS"),sQuery(id+"F0.wireOp",EDGE,"E91.MirrorCS"),sQuery(id+"F0.wireOp",EDGE,"E92.MirrorCS"),sQuery(id+"F0.wireOp",EDGE,"E93.MirrorCS"),sQuery(id+"F0.wireOp",EDGE,"E94.MirrorCS"),sQuery(id+"F0.wireOp",EDGE,"E95.MirrorCS"),sQuery(id+"F0.wireOp",EDGE,"E96.MirrorCS"),sQuery(id+"F0.wireOp",EDGE,"E97.MirrorCS"),sQuery(id+"F0.wireOp",EDGE,"E98.MirrorCS"),sQuery(id+"F0.wireOp",EDGE,"E99.MirrorCS"),sQuery(id+"F0.wireOp",EDGE,"E100.MirrorCS"),sQuery(id+"F0.wireOp",EDGE,"E101.MirrorCS"),sQuery(id+"F0.wireOp",EDGE,"E102.MirrorCS"),sQuery(id+"F0.wireOp",EDGE,"E103.MirrorCS"),sQuery(id+"F0.wireOp",EDGE,"E104.MirrorCS"),sQuery(id+"F0.wireOp",EDGE,"E105.MirrorCS"),sQuery(id+"F0.wireOp",EDGE,"E106.MirrorCS"),sQuery(id+"F0.wireOp",EDGE,"E107.MirrorCS"),sQuery(id+"F0.wireOp",EDGE,"E108.MirrorCS"),sQuery(id+"F0.wireOp",EDGE,"E109.MirrorCS"),sQuery(id+"F0.wireOp",EDGE,"E111.MirrorCS"),sQuery(id+"F0.wireOp",EDGE,"E112.MirrorCS"),sQuery(id+"F0.wireOp",EDGE,"E113.MirrorCS"),sQuery(id+"F0.wireOp",EDGE,"E114.MirrorCS")])],"isStart":true});
            extrude(context, id + "F4", {"entities" : qUnion([Q0, Q1, Q2]), "operationType" : NewBodyOperationType.ADD, "endBound" : BoundingType.UP_TO_SURFACE, "oppositeDirection" : true, "depth" : 25 * mm, "endBoundEntityFace" : qUnion([Q3]), "offsetDistance" : 25 * mm});
        }
        {
            var Q0;
            Q0=makeQuery(id+"F3.imprint","IMPRINT",FACE,{"disambiguationData":[TD([[makeQuery(id+"F3.imprint","IMPRINT",EDGE,{"derivedFrom":sQuery(id+"F3.wireOp",EDGE,"E124.sketch_text.stroke-40")}),1.0]])]});
            var Q1;
            {var subQ0=sQuery(id+"F0.wireOp",EDGE,"E114.MirrorCS");var subQ1=sQuery(id+"F0.wireOp",EDGE,"E113.MirrorCS");var subQ2=sQuery(id+"F0.wireOp",EDGE,"E112.MirrorCS");var subQ3=sQuery(id+"F0.wireOp",EDGE,"E111.MirrorCS");var subQ4=sQuery(id+"F0.wireOp",EDGE,"E109.MirrorCS");var subQ5=sQuery(id+"F0.wireOp",EDGE,"E108.MirrorCS");var subQ6=sQuery(id+"F0.wireOp",EDGE,"E107.MirrorCS");var subQ7=sQuery(id+"F0.wireOp",EDGE,"E106.MirrorCS");var subQ8=sQuery(id+"F0.wireOp",EDGE,"E105.MirrorCS");var subQ9=sQuery(id+"F0.wireOp",EDGE,"E104.MirrorCS");var subQ10=sQuery(id+"F0.wireOp",EDGE,"E103.MirrorCS");var subQ11=sQuery(id+"F0.wireOp",EDGE,"E102.MirrorCS");var subQ12=sQuery(id+"F0.wireOp",EDGE,"E101.MirrorCS");var subQ13=sQuery(id+"F0.wireOp",EDGE,"E100.MirrorCS");var subQ14=sQuery(id+"F0.wireOp",EDGE,"E99.MirrorCS");var subQ15=sQuery(id+"F0.wireOp",EDGE,"E98.MirrorCS");var subQ16=sQuery(id+"F0.wireOp",EDGE,"E97.MirrorCS");var subQ17=sQuery(id+"F0.wireOp",EDGE,"E96.MirrorCS");var subQ18=sQuery(id+"F0.wireOp",EDGE,"E95.MirrorCS");var subQ19=sQuery(id+"F0.wireOp",EDGE,"E94.MirrorCS");var subQ20=sQuery(id+"F0.wireOp",EDGE,"E93.MirrorCS");var subQ21=sQuery(id+"F0.wireOp",EDGE,"E92.MirrorCS");var subQ22=sQuery(id+"F0.wireOp",EDGE,"E91.MirrorCS");var subQ23=sQuery(id+"F0.wireOp",EDGE,"E90.MirrorCS");var subQ24=sQuery(id+"F0.wireOp",EDGE,"E89.MirrorCS");var subQ25=sQuery(id+"F0.wireOp",EDGE,"E88.MirrorCS");var subQ26=sQuery(id+"F0.wireOp",EDGE,"E87.MirrorCS");var subQ27=sQuery(id+"F0.wireOp",EDGE,"E86.MirrorCS");var subQ28=sQuery(id+"F0.wireOp",EDGE,"E85.MirrorCS");var subQ29=sQuery(id+"F0.wireOp",EDGE,"E84.MirrorCS");var subQ30=sQuery(id+"F0.wireOp",EDGE,"E83.MirrorCS");var subQ31=sQuery(id+"F0.wireOp",EDGE,"E82.MirrorCS");var subQ32=sQuery(id+"F0.wireOp",EDGE,"E81.MirrorCS");var subQ33=sQuery(id+"F0.wireOp",EDGE,"E80.MirrorCS");var subQ34=sQuery(id+"F0.wireOp",EDGE,"E79.MirrorCS");var subQ35=sQuery(id+"F0.wireOp",EDGE,"E78.MirrorCS");var subQ36=sQuery(id+"F0.wireOp",EDGE,"E77.MirrorCS");var subQ37=sQuery(id+"F0.wireOp",EDGE,"E76.MirrorCS");var subQ38=sQuery(id+"F0.wireOp",EDGE,"E75.MirrorCS");var subQ39=sQuery(id+"F0.wireOp",EDGE,"E74.MirrorCS");var subQ40=sQuery(id+"F0.wireOp",EDGE,"E73.MirrorCS");var subQ41=sQuery(id+"F0.wireOp",EDGE,"E72.MirrorCS");var subQ42=sQuery(id+"F0.wireOp",EDGE,"E71.MirrorCS");var subQ43=sQuery(id+"F0.wireOp",EDGE,"E70.MirrorCS");var subQ44=sQuery(id+"F0.wireOp",EDGE,"E69.MirrorCS");var subQ45=sQuery(id+"F0.wireOp",EDGE,"E68.MirrorCS");var subQ46=sQuery(id+"F0.wireOp",EDGE,"E67.MirrorCS");var subQ47=sQuery(id+"F0.wireOp",EDGE,"E66.MirrorCS");var subQ48=sQuery(id+"F0.wireOp",EDGE,"E65.MirrorCS");var subQ49=sQuery(id+"F0.wireOp",EDGE,"E64.MirrorCS");var subQ50=sQuery(id+"F0.wireOp",EDGE,"E63.MirrorCS");var subQ51=sQuery(id+"F0.wireOp",EDGE,"E62.MirrorCS");var subQ52=sQuery(id+"F0.wireOp",EDGE,"E61.MirrorCS");var subQ53=sQuery(id+"F0.wireOp",EDGE,"E60.MirrorCS");var subQ54=sQuery(id+"F0.wireOp",EDGE,"E59.MirrorCS");var subQ55=sQuery(id+"F0.wireOp",EDGE,"E58.MirrorCS");var subQ56=sQuery(id+"F0.wireOp",EDGE,"E57");var subQ57=sQuery(id+"F0.wireOp",EDGE,"E56");var subQ58=sQuery(id+"F0.wireOp",EDGE,"E55");var subQ59=sQuery(id+"F0.wireOp",EDGE,"E54");var subQ60=sQuery(id+"F0.wireOp",EDGE,"E53");var subQ61=sQuery(id+"F0.wireOp",EDGE,"E52");var subQ62=sQuery(id+"F0.wireOp",EDGE,"E51");var subQ63=sQuery(id+"F0.wireOp",EDGE,"E50");var subQ64=sQuery(id+"F0.wireOp",EDGE,"E49");var subQ65=sQuery(id+"F0.wireOp",EDGE,"E48");var subQ66=sQuery(id+"F0.wireOp",EDGE,"E47");var subQ67=sQuery(id+"F0.wireOp",EDGE,"E46");var subQ68=sQuery(id+"F0.wireOp",EDGE,"E45");var subQ69=sQuery(id+"F0.wireOp",EDGE,"E44");var subQ70=sQuery(id+"F0.wireOp",EDGE,"E43");var subQ71=sQuery(id+"F0.wireOp",EDGE,"E42");var subQ72=sQuery(id+"F0.wireOp",EDGE,"E41");var subQ73=sQuery(id+"F0.wireOp",EDGE,"E40");var subQ74=sQuery(id+"F0.wireOp",EDGE,"E39");var subQ75=sQuery(id+"F0.wireOp",EDGE,"E38");var subQ76=sQuery(id+"F0.wireOp",EDGE,"E37");var subQ77=sQuery(id+"F0.wireOp",EDGE,"E36");var subQ78=sQuery(id+"F0.wireOp",EDGE,"E35");var subQ79=sQuery(id+"F0.wireOp",EDGE,"E34");var subQ80=sQuery(id+"F0.wireOp",EDGE,"E33");var subQ81=sQuery(id+"F0.wireOp",EDGE,"E32");var subQ82=sQuery(id+"F0.wireOp",EDGE,"E31");var subQ83=sQuery(id+"F0.wireOp",EDGE,"E30.MirrorCS");var subQ84=sQuery(id+"F0.wireOp",EDGE,"E29.MirrorCS");var subQ85=sQuery(id+"F0.wireOp",EDGE,"E28.MirrorCS");var subQ86=sQuery(id+"F0.wireOp",EDGE,"E27.MirrorCS");var subQ87=sQuery(id+"F0.wireOp",EDGE,"E26.MirrorCS");var subQ88=sQuery(id+"F0.wireOp",EDGE,"E25.MirrorCS");var subQ89=sQuery(id+"F0.wireOp",EDGE,"E24");var subQ90=sQuery(id+"F0.wireOp",EDGE,"E23");var subQ91=sQuery(id+"F0.wireOp",EDGE,"E22");var subQ92=sQuery(id+"F0.wireOp",EDGE,"E21");var subQ93=sQuery(id+"F0.wireOp",EDGE,"E20");var subQ94=sQuery(id+"F0.wireOp",EDGE,"E19");var subQ95=sQuery(id+"F0.wireOp",EDGE,"E17");var subQ96=sQuery(id+"F0.wireOp",EDGE,"E16");var subQ97=sQuery(id+"F0.wireOp",EDGE,"E15");var subQ98=sQuery(id+"F0.wireOp",EDGE,"E14");var subQ99=sQuery(id+"F0.wireOp",EDGE,"E13");var subQ100=sQuery(id+"F0.wireOp",EDGE,"E11");var subQ101=sQuery(id+"F0.wireOp",EDGE,"E10");var subQ102=sQuery(id+"F0.wireOp",EDGE,"E9");var subQ103=sQuery(id+"F0.wireOp",EDGE,"E8");var subQ104=sQuery(id+"F0.wireOp",EDGE,"E7");var subQ105=sQuery(id+"F0.wireOp",EDGE,"E6");var subQ106=sQuery(id+"F0.wireOp",EDGE,"E5");var subQ107=sQuery(id+"F0.wireOp",EDGE,"E4");var subQ108=sQuery(id+"F0.wireOp",EDGE,"E3");var subQ109=sQuery(id+"F0.wireOp",EDGE,"E2");var subQ110=sQuery(id+"F0.wireOp",EDGE,"E1");var subQ111=sQuery(id+"F0.wireOp",EDGE,"E0");Q1=makeQuery(id+"F4.boolean.opBoolean","MERGE",FACE,{"derivedFrom":[makeQuery(id+"F1.opExtrude","CAP_FACE",FACE,{"disambiguationData":[OSD([subQ111,subQ110,subQ109,subQ108,subQ107,subQ106,subQ105,subQ104,subQ103,subQ102,subQ101,subQ100,subQ99,subQ98,subQ97,subQ96,subQ95,subQ94,subQ93,subQ92,subQ91,subQ90,subQ89,subQ88,subQ87,subQ86,subQ85,subQ84,subQ83,subQ82,subQ81,subQ80,subQ79,subQ78,subQ77,subQ76,subQ75,subQ74,subQ73,subQ72,subQ71,subQ70,subQ69,subQ68,subQ67,subQ66,subQ65,subQ64,subQ63,subQ62,subQ61,subQ60,subQ59,subQ58,subQ57,subQ56,subQ55,subQ54,subQ53,subQ52,subQ51,subQ50,subQ49,subQ48,subQ47,subQ46,subQ45,subQ44,subQ43,subQ42,subQ41,subQ40,subQ39,subQ38,subQ37,subQ36,subQ35,subQ34,subQ33,subQ32,subQ31,subQ30,subQ29,subQ28,subQ27,subQ26,subQ25,subQ24,subQ23,subQ22,subQ21,subQ20,subQ19,subQ18,subQ17,subQ16,subQ15,subQ14,subQ13,subQ12,subQ11,subQ10,subQ9,subQ8,subQ7,subQ6,subQ5,subQ4,subQ3,subQ2,subQ1,subQ0])],"isStart":true}),makeQuery(id+"F4.opExtrude","CAP_FACE",FACE,{"disambiguationData":[OSD([subQ111,subQ110,subQ109,subQ108,subQ107,subQ106,subQ105,subQ104,subQ103,subQ102,subQ101,subQ100,subQ99,subQ98,subQ97,subQ96,subQ95,subQ94,subQ93,subQ92,subQ91,subQ90,subQ89,subQ88,subQ87,subQ86,subQ85,subQ84,subQ83,subQ82,subQ81,subQ80,subQ79,subQ78,subQ77,subQ76,subQ75,subQ74,subQ73,subQ72,subQ71,subQ70,subQ69,subQ68,subQ67,subQ66,subQ65,subQ64,subQ63,subQ62,subQ61,subQ60,subQ59,subQ58,subQ57,subQ56,subQ55,subQ54,subQ53,subQ52,subQ51,subQ50,subQ49,subQ48,subQ47,subQ46,subQ45,subQ44,subQ43,subQ42,subQ41,subQ40,subQ39,subQ38,subQ37,subQ36,subQ35,subQ34,subQ33,subQ32,subQ31,subQ30,subQ29,subQ28,subQ27,subQ26,subQ25,subQ24,subQ23,subQ22,subQ21,subQ20,subQ19,subQ18,subQ17,subQ16,subQ15,subQ14,subQ13,subQ12,subQ11,subQ10,subQ9,subQ8,subQ7,subQ6,subQ5,subQ4,subQ3,subQ2,subQ1,subQ0])],"isStart":false})]});}
            extrude(context, id + "F5", {"entities" : qUnion([Q0]), "endBound" : BoundingType.UP_TO_SURFACE, "oppositeDirection" : true, "depth" : 25 * mm, "endBoundEntityFace" : qUnion([Q1]), "offsetDistance" : 25 * mm});
        }
        {
            var Q0;
            Q0=makeQuery(id+"F3.imprint","IMPRINT",FACE,{"disambiguationData":[TD([[makeQuery(id+"F3.imprint","IMPRINT",EDGE,{"derivedFrom":sQuery(id+"F3.wireOp",EDGE,"E115.top")}),-1.0]])]});
            var sketch = newSketch(context, id + "F6", { "sketchPlane" : qUnion([Q0])});
            skLineSegment(sketch, "E129.bottom", {"start": v(1.1, -47.25) * mm, "end": v(2.4, -47.25) * mm});
            skLineSegment(sketch, "E129.top", {"start": v(1.1, -53.65) * mm, "end": v(2.4, -53.65) * mm});
            skLineSegment(sketch, "E129.left", {"start": v(1.1, -47.25) * mm, "end": v(1.1, -53.65) * mm});
            skLineSegment(sketch, "E129.right", {"start": v(2.4, -47.25) * mm, "end": v(2.4, -53.65) * mm});
            skSolve(sketch);
        }
        {
            var Q0;
            Q0 = qSketchRegion(id + "F6", true);
            var Q1;
            {var subQ0=sQuery(id+"F0.wireOp",EDGE,"E114.MirrorCS");var subQ1=sQuery(id+"F0.wireOp",EDGE,"E113.MirrorCS");var subQ2=sQuery(id+"F0.wireOp",EDGE,"E112.MirrorCS");var subQ3=sQuery(id+"F0.wireOp",EDGE,"E111.MirrorCS");var subQ4=sQuery(id+"F0.wireOp",EDGE,"E109.MirrorCS");var subQ5=sQuery(id+"F0.wireOp",EDGE,"E108.MirrorCS");var subQ6=sQuery(id+"F0.wireOp",EDGE,"E107.MirrorCS");var subQ7=sQuery(id+"F0.wireOp",EDGE,"E106.MirrorCS");var subQ8=sQuery(id+"F0.wireOp",EDGE,"E105.MirrorCS");var subQ9=sQuery(id+"F0.wireOp",EDGE,"E104.MirrorCS");var subQ10=sQuery(id+"F0.wireOp",EDGE,"E103.MirrorCS");var subQ11=sQuery(id+"F0.wireOp",EDGE,"E102.MirrorCS");var subQ12=sQuery(id+"F0.wireOp",EDGE,"E101.MirrorCS");var subQ13=sQuery(id+"F0.wireOp",EDGE,"E100.MirrorCS");var subQ14=sQuery(id+"F0.wireOp",EDGE,"E99.MirrorCS");var subQ15=sQuery(id+"F0.wireOp",EDGE,"E98.MirrorCS");var subQ16=sQuery(id+"F0.wireOp",EDGE,"E97.MirrorCS");var subQ17=sQuery(id+"F0.wireOp",EDGE,"E96.MirrorCS");var subQ18=sQuery(id+"F0.wireOp",EDGE,"E95.MirrorCS");var subQ19=sQuery(id+"F0.wireOp",EDGE,"E94.MirrorCS");var subQ20=sQuery(id+"F0.wireOp",EDGE,"E93.MirrorCS");var subQ21=sQuery(id+"F0.wireOp",EDGE,"E92.MirrorCS");var subQ22=sQuery(id+"F0.wireOp",EDGE,"E91.MirrorCS");var subQ23=sQuery(id+"F0.wireOp",EDGE,"E90.MirrorCS");var subQ24=sQuery(id+"F0.wireOp",EDGE,"E89.MirrorCS");var subQ25=sQuery(id+"F0.wireOp",EDGE,"E88.MirrorCS");var subQ26=sQuery(id+"F0.wireOp",EDGE,"E87.MirrorCS");var subQ27=sQuery(id+"F0.wireOp",EDGE,"E86.MirrorCS");var subQ28=sQuery(id+"F0.wireOp",EDGE,"E85.MirrorCS");var subQ29=sQuery(id+"F0.wireOp",EDGE,"E84.MirrorCS");var subQ30=sQuery(id+"F0.wireOp",EDGE,"E83.MirrorCS");var subQ31=sQuery(id+"F0.wireOp",EDGE,"E82.MirrorCS");var subQ32=sQuery(id+"F0.wireOp",EDGE,"E81.MirrorCS");var subQ33=sQuery(id+"F0.wireOp",EDGE,"E80.MirrorCS");var subQ34=sQuery(id+"F0.wireOp",EDGE,"E79.MirrorCS");var subQ35=sQuery(id+"F0.wireOp",EDGE,"E78.MirrorCS");var subQ36=sQuery(id+"F0.wireOp",EDGE,"E77.MirrorCS");var subQ37=sQuery(id+"F0.wireOp",EDGE,"E76.MirrorCS");var subQ38=sQuery(id+"F0.wireOp",EDGE,"E75.MirrorCS");var subQ39=sQuery(id+"F0.wireOp",EDGE,"E74.MirrorCS");var subQ40=sQuery(id+"F0.wireOp",EDGE,"E73.MirrorCS");var subQ41=sQuery(id+"F0.wireOp",EDGE,"E72.MirrorCS");var subQ42=sQuery(id+"F0.wireOp",EDGE,"E71.MirrorCS");var subQ43=sQuery(id+"F0.wireOp",EDGE,"E70.MirrorCS");var subQ44=sQuery(id+"F0.wireOp",EDGE,"E69.MirrorCS");var subQ45=sQuery(id+"F0.wireOp",EDGE,"E68.MirrorCS");var subQ46=sQuery(id+"F0.wireOp",EDGE,"E67.MirrorCS");var subQ47=sQuery(id+"F0.wireOp",EDGE,"E66.MirrorCS");var subQ48=sQuery(id+"F0.wireOp",EDGE,"E65.MirrorCS");var subQ49=sQuery(id+"F0.wireOp",EDGE,"E64.MirrorCS");var subQ50=sQuery(id+"F0.wireOp",EDGE,"E63.MirrorCS");var subQ51=sQuery(id+"F0.wireOp",EDGE,"E62.MirrorCS");var subQ52=sQuery(id+"F0.wireOp",EDGE,"E61.MirrorCS");var subQ53=sQuery(id+"F0.wireOp",EDGE,"E60.MirrorCS");var subQ54=sQuery(id+"F0.wireOp",EDGE,"E59.MirrorCS");var subQ55=sQuery(id+"F0.wireOp",EDGE,"E58.MirrorCS");var subQ56=sQuery(id+"F0.wireOp",EDGE,"E57");var subQ57=sQuery(id+"F0.wireOp",EDGE,"E56");var subQ58=sQuery(id+"F0.wireOp",EDGE,"E55");var subQ59=sQuery(id+"F0.wireOp",EDGE,"E54");var subQ60=sQuery(id+"F0.wireOp",EDGE,"E53");var subQ61=sQuery(id+"F0.wireOp",EDGE,"E52");var subQ62=sQuery(id+"F0.wireOp",EDGE,"E51");var subQ63=sQuery(id+"F0.wireOp",EDGE,"E50");var subQ64=sQuery(id+"F0.wireOp",EDGE,"E49");var subQ65=sQuery(id+"F0.wireOp",EDGE,"E48");var subQ66=sQuery(id+"F0.wireOp",EDGE,"E47");var subQ67=sQuery(id+"F0.wireOp",EDGE,"E46");var subQ68=sQuery(id+"F0.wireOp",EDGE,"E45");var subQ69=sQuery(id+"F0.wireOp",EDGE,"E44");var subQ70=sQuery(id+"F0.wireOp",EDGE,"E43");var subQ71=sQuery(id+"F0.wireOp",EDGE,"E42");var subQ72=sQuery(id+"F0.wireOp",EDGE,"E41");var subQ73=sQuery(id+"F0.wireOp",EDGE,"E40");var subQ74=sQuery(id+"F0.wireOp",EDGE,"E39");var subQ75=sQuery(id+"F0.wireOp",EDGE,"E38");var subQ76=sQuery(id+"F0.wireOp",EDGE,"E37");var subQ77=sQuery(id+"F0.wireOp",EDGE,"E36");var subQ78=sQuery(id+"F0.wireOp",EDGE,"E35");var subQ79=sQuery(id+"F0.wireOp",EDGE,"E34");var subQ80=sQuery(id+"F0.wireOp",EDGE,"E33");var subQ81=sQuery(id+"F0.wireOp",EDGE,"E32");var subQ82=sQuery(id+"F0.wireOp",EDGE,"E31");var subQ83=sQuery(id+"F0.wireOp",EDGE,"E30.MirrorCS");var subQ84=sQuery(id+"F0.wireOp",EDGE,"E29.MirrorCS");var subQ85=sQuery(id+"F0.wireOp",EDGE,"E28.MirrorCS");var subQ86=sQuery(id+"F0.wireOp",EDGE,"E27.MirrorCS");var subQ87=sQuery(id+"F0.wireOp",EDGE,"E26.MirrorCS");var subQ88=sQuery(id+"F0.wireOp",EDGE,"E25.MirrorCS");var subQ89=sQuery(id+"F0.wireOp",EDGE,"E24");var subQ90=sQuery(id+"F0.wireOp",EDGE,"E23");var subQ91=sQuery(id+"F0.wireOp",EDGE,"E22");var subQ92=sQuery(id+"F0.wireOp",EDGE,"E21");var subQ93=sQuery(id+"F0.wireOp",EDGE,"E20");var subQ94=sQuery(id+"F0.wireOp",EDGE,"E19");var subQ95=sQuery(id+"F0.wireOp",EDGE,"E17");var subQ96=sQuery(id+"F0.wireOp",EDGE,"E16");var subQ97=sQuery(id+"F0.wireOp",EDGE,"E15");var subQ98=sQuery(id+"F0.wireOp",EDGE,"E14");var subQ99=sQuery(id+"F0.wireOp",EDGE,"E13");var subQ100=sQuery(id+"F0.wireOp",EDGE,"E11");var subQ101=sQuery(id+"F0.wireOp",EDGE,"E10");var subQ102=sQuery(id+"F0.wireOp",EDGE,"E9");var subQ103=sQuery(id+"F0.wireOp",EDGE,"E8");var subQ104=sQuery(id+"F0.wireOp",EDGE,"E7");var subQ105=sQuery(id+"F0.wireOp",EDGE,"E6");var subQ106=sQuery(id+"F0.wireOp",EDGE,"E5");var subQ107=sQuery(id+"F0.wireOp",EDGE,"E4");var subQ108=sQuery(id+"F0.wireOp",EDGE,"E3");var subQ109=sQuery(id+"F0.wireOp",EDGE,"E2");var subQ110=sQuery(id+"F0.wireOp",EDGE,"E1");var subQ111=sQuery(id+"F0.wireOp",EDGE,"E0");Q1=makeQuery(id+"F4.boolean.opBoolean","MERGE",FACE,{"derivedFrom":[makeQuery(id+"F1.opExtrude","CAP_FACE",FACE,{"disambiguationData":[OSD([subQ111,subQ110,subQ109,subQ108,subQ107,subQ106,subQ105,subQ104,subQ103,subQ102,subQ101,subQ100,subQ99,subQ98,subQ97,subQ96,subQ95,subQ94,subQ93,subQ92,subQ91,subQ90,subQ89,subQ88,subQ87,subQ86,subQ85,subQ84,subQ83,subQ82,subQ81,subQ80,subQ79,subQ78,subQ77,subQ76,subQ75,subQ74,subQ73,subQ72,subQ71,subQ70,subQ69,subQ68,subQ67,subQ66,subQ65,subQ64,subQ63,subQ62,subQ61,subQ60,subQ59,subQ58,subQ57,subQ56,subQ55,subQ54,subQ53,subQ52,subQ51,subQ50,subQ49,subQ48,subQ47,subQ46,subQ45,subQ44,subQ43,subQ42,subQ41,subQ40,subQ39,subQ38,subQ37,subQ36,subQ35,subQ34,subQ33,subQ32,subQ31,subQ30,subQ29,subQ28,subQ27,subQ26,subQ25,subQ24,subQ23,subQ22,subQ21,subQ20,subQ19,subQ18,subQ17,subQ16,subQ15,subQ14,subQ13,subQ12,subQ11,subQ10,subQ9,subQ8,subQ7,subQ6,subQ5,subQ4,subQ3,subQ2,subQ1,subQ0])],"isStart":true}),makeQuery(id+"F4.opExtrude","CAP_FACE",FACE,{"disambiguationData":[OSD([subQ111,subQ110,subQ109,subQ108,subQ107,subQ106,subQ105,subQ104,subQ103,subQ102,subQ101,subQ100,subQ99,subQ98,subQ97,subQ96,subQ95,subQ94,subQ93,subQ92,subQ91,subQ90,subQ89,subQ88,subQ87,subQ86,subQ85,subQ84,subQ83,subQ82,subQ81,subQ80,subQ79,subQ78,subQ77,subQ76,subQ75,subQ74,subQ73,subQ72,subQ71,subQ70,subQ69,subQ68,subQ67,subQ66,subQ65,subQ64,subQ63,subQ62,subQ61,subQ60,subQ59,subQ58,subQ57,subQ56,subQ55,subQ54,subQ53,subQ52,subQ51,subQ50,subQ49,subQ48,subQ47,subQ46,subQ45,subQ44,subQ43,subQ42,subQ41,subQ40,subQ39,subQ38,subQ37,subQ36,subQ35,subQ34,subQ33,subQ32,subQ31,subQ30,subQ29,subQ28,subQ27,subQ26,subQ25,subQ24,subQ23,subQ22,subQ21,subQ20,subQ19,subQ18,subQ17,subQ16,subQ15,subQ14,subQ13,subQ12,subQ11,subQ10,subQ9,subQ8,subQ7,subQ6,subQ5,subQ4,subQ3,subQ2,subQ1,subQ0])],"isStart":false})]});}
            extrude(context, id + "F7", {"entities" : qUnion([Q0]), "operationType" : NewBodyOperationType.ADD, "endBound" : BoundingType.UP_TO_SURFACE, "oppositeDirection" : true, "depth" : 25 * mm, "endBoundEntityFace" : qUnion([Q1]), "offsetDistance" : 25 * mm});
        }
        {
            var Q0;
            Q0=makeQuery(id+"F4.opExtrude","SWEPT_EDGE",EDGE,{"disambiguationData":[OSD([sQuery(id+"F3.wireOp",EDGE,"E117"),sQuery(id+"F3.wireOp",EDGE,"E118")])]});
            var Q1;
            Q1=makeQuery(id+"F4.opExtrude","SWEPT_EDGE",EDGE,{"disambiguationData":[OSD([sQuery(id+"F3.wireOp",EDGE,"E118"),sQuery(id+"F3.wireOp",EDGE,"E119")])]});
            var Q2;
            Q2=makeQuery(id+"F4.opExtrude","SWEPT_EDGE",EDGE,{"disambiguationData":[OSD([sQuery(id+"F3.wireOp",EDGE,"E119"),sQuery(id+"F3.wireOp",EDGE,"E123")])]});
            var Q3;
            Q3=makeQuery(id+"F4.opExtrude","SWEPT_EDGE",EDGE,{"disambiguationData":[OSD([sQuery(id+"F3.wireOp",EDGE,"E121.MirrorCS"),sQuery(id+"F3.wireOp",EDGE,"E122.MirrorCS")])]});
            var Q4;
            Q4=makeQuery(id+"F4.opExtrude","SWEPT_EDGE",EDGE,{"disambiguationData":[OSD([sQuery(id+"F3.wireOp",EDGE,"E122.MirrorCS"),sQuery(id+"F3.wireOp",EDGE,"E123")])]});
            var Q5;
            Q5=makeQuery(id+"F4.opExtrude","SWEPT_EDGE",EDGE,{"disambiguationData":[OSD([sQuery(id+"F3.wireOp",EDGE,"E120.MirrorCS"),sQuery(id+"F3.wireOp",EDGE,"E121.MirrorCS")])]});
            var Q6;
            Q6=makeQuery(id+"F4.opExtrude","SWEPT_EDGE",EDGE,{"disambiguationData":[OSD([sQuery(id+"F3.wireOp",EDGE,"E128.1"),sQuery(id+"F3.wireOp",EDGE,"E128.2")])]});
            var Q7;
            Q7=makeQuery(id+"F4.opExtrude","SWEPT_EDGE",EDGE,{"disambiguationData":[OSD([sQuery(id+"F3.wireOp",EDGE,"E128.0"),sQuery(id+"F3.wireOp",EDGE,"E128.1")])]});
            fillet(context, id + "F8", {"entities" : qUnion([Q0, Q1, Q2, Q3, Q4, Q5, Q6, Q7]), "radius" : 5 * mm, "tangentPropagation" : true, "allowEdgeOverflow" : false});
        }
        {
            var Q0;
            Q0=makeQuery(id+"F4.opExtrude","SWEPT_EDGE",EDGE,{"disambiguationData":[OSD([sQuery(id+"F3.wireOp",EDGE,"E125"),sQuery(id+"F3.wireOp",EDGE,"E126")])]});
            var Q1;
            Q1=makeQuery(id+"F4.opExtrude","SWEPT_EDGE",EDGE,{"disambiguationData":[OSD([sQuery(id+"F3.wireOp",EDGE,"E126"),sQuery(id+"F3.wireOp",EDGE,"E127")])]});
            fillet(context, id + "F9", {"entities" : qUnion([Q0, Q1]), "radius" : 15 * mm, "tangentPropagation" : true, "allowEdgeOverflow" : false});
        }
        {
            var Q0;
            Q0=qCreatedBy(makeId("Right.planeOp"),FACE);
            var sketch = newSketch(context, id + "F10", { "sketchPlane" : qUnion([Q0])});
            skLineSegment(sketch, "E130.bottom", {"start": v(-2, 42.58) * mm, "end": v(0, 42.58) * mm});
            skLineSegment(sketch, "E130.top", {"start": v(-2, -96.17) * mm, "end": v(0, -96.17) * mm});
            skLineSegment(sketch, "E130.left", {"start": v(-2, 42.58) * mm, "end": v(-2, -96.17) * mm});
            skLineSegment(sketch, "E130.right", {"start": v(0, 42.58) * mm, "end": v(0, -96.17) * mm});
            skLineSegment(sketch, "E131.bottom", {"start": v(0, -96.17) * mm, "end": v(0.46, -96.17) * mm});
            skLineSegment(sketch, "E131.top", {"start": v(0, 42.58) * mm, "end": v(0.46, 42.58) * mm});
            skLineSegment(sketch, "E131.left", {"start": v(0, -96.17) * mm, "end": v(0, 42.58) * mm});
            skLineSegment(sketch, "E131.right", {"start": v(0.46, -96.17) * mm, "end": v(0.46, 42.58) * mm});
            skSolve(sketch);
        }
        {
            var Q0;
            Q0=makeQuery(id+"F10.imprint","IMPRINT",FACE,{"disambiguationData":[TD([[makeQuery(id+"F10.imprint","IMPRINT",EDGE,{"derivedFrom":sQuery(id+"F10.wireOp",EDGE,"E131.bottom")}),1.0]])]});
            extrude(context, id + "F11", {"entities" : qUnion([Q0]), "operationType" : NewBodyOperationType.REMOVE, "endBound" : BoundingType.THROUGH_ALL, "oppositeDirection" : true, "depth" : 25 * mm, "offsetDistance" : 25 * mm, "hasSecondDirection" : true, "secondDirectionBound" : SecondDirectionBoundingType.THROUGH_ALL, "secondDirectionOppositeDirection" : false, "secondDirectionDepth" : 25 * mm});
        }
    });
